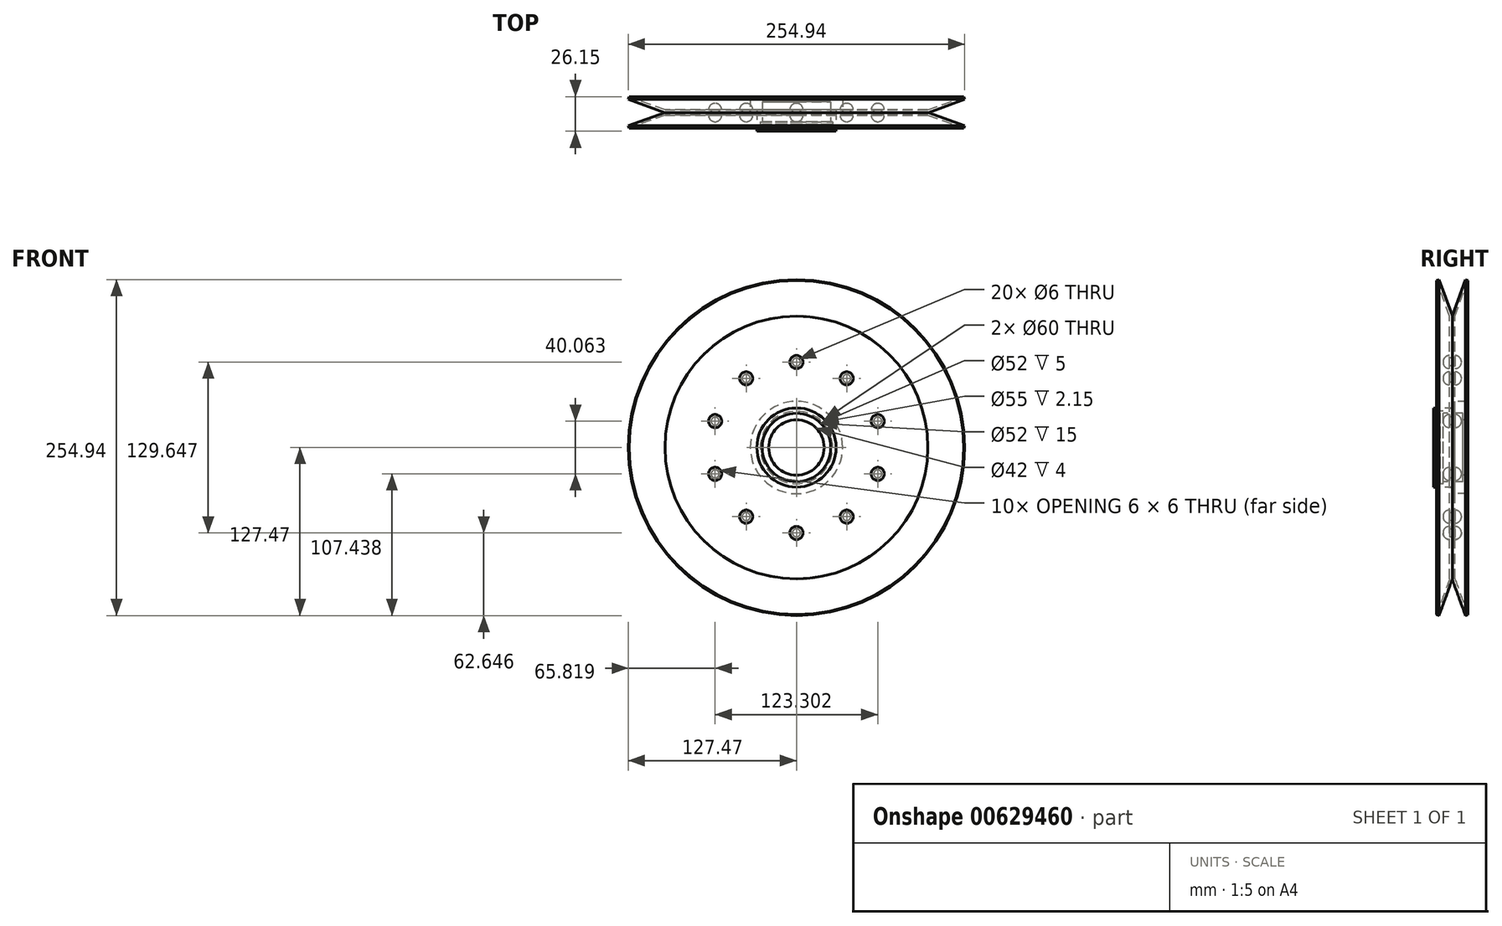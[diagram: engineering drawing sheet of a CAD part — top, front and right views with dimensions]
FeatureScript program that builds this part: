
annotation { "Feature Type Name" : "Feature", "Feature Type Description" : "" }
export const myFeature = defineFeature(function(context is Context, id is Id, definition is map)
    precondition{}
    {
        {
            var Q0;
            Q0=qCreatedBy(makeId("Right.planeOp"),FACE);
            var sketch = newSketch(context, id + "F0", { "sketchPlane" : qUnion([Q0])});
            skLineSegment(sketch, "E0", {"start": v(0, 0) * mm, "end": v(0, 100) * mm});
            skLineSegment(sketch, "E1", {"start": v(0, 100) * mm, "end": v(10, 127.47) * mm});
            skLineSegment(sketch, "E2.0", {"start": v(2, 99.65) * mm, "end": v(11.88, 126.8) * mm});
            skLineSegment(sketch, "E2.1", {"start": v(2, 0) * mm, "end": v(2, 99.65) * mm});
            skLineSegment(sketch, "E3", {"start": v(10, 127.47) * mm, "end": v(11.88, 126.8) * mm});
            skLineSegment(sketch, "E4", {"start": v(0, 0) * mm, "end": v(2, 0) * mm});
            skSolve(sketch);
        }
        {
            var Q0;
            Q0=makeQuery(id+"F0.imprint","IMPRINT",FACE,{"disambiguationData":[TD([[makeQuery(id+"F0.imprint","IMPRINT",EDGE,{"derivedFrom":sQuery(id+"F0.wireOp",EDGE,"E0")}),-1.0]])]});
            var Q1;
            Q1=sQuery(id+"F0.wireOp",EDGE,"E4");
            revolve(context, id + "F1", {"surfaceOperationType" : NewSurfaceOperationType.NEW, "entities" : qUnion([Q0]), "axis" : qUnion([Q1]), "revolveType" : RevolveType.FULL});
        }
        {
            var Q0;
            Q0=makeQuery(id+"F1.opRevolve","SWEPT_FACE",FACE,{"disambiguationData":[OSD([sQuery(id+"F0.wireOp",EDGE,"E2.1")])]});
            var sketch = newSketch(context, id + "F2", { "sketchPlane" : qUnion([Q0])});
            skPoint(sketch, "E5", {"position": v(0, 0) * mm});
            skSolve(sketch);
        }
        {
            var Q0;
            Q0=sQuery(id+"F2.wireOp",VERTEX,"E5");
            var Q1;
            Q1=makeQuery(id+"F1.opRevolve","SWEPT_BODY",BODY,{"disambiguationData":[OSD([sQuery(id+"F0.wireOp",EDGE,"E0"),sQuery(id+"F0.wireOp",EDGE,"E1"),sQuery(id+"F0.wireOp",EDGE,"E2.0"),sQuery(id+"F0.wireOp",EDGE,"E2.1"),sQuery(id+"F0.wireOp",EDGE,"E3"),sQuery(id+"F0.wireOp",EDGE,"E4")])]});
            hole(context, id + "F3", {"style" : HoleStyle.SIMPLE, "endStyle" : HoleEndStyle.THROUGH, "holeDiameter" : 60 * mm, "majorDiameter" : 10 * mm, "isTappedThrough" : true, "tappedDepth" : 25.5 * mm, "tapClearance" : 3, "locations" : qUnion([Q0]), "scope" : qUnion([Q1]), "startStyle" : HoleStartStyle.SKETCH});
        }
        {
            var Q0;
            Q0=makeQuery(id+"F1.opRevolve","SWEPT_FACE",FACE,{"disambiguationData":[OSD([sQuery(id+"F0.wireOp",EDGE,"E2.1")])]});
            var sketch = newSketch(context, id + "F4", { "sketchPlane" : qUnion([Q0])});
            skCircle(sketch, "E6.0.0", {"center": v(0, 0) * mm, "radius": 99.65 * mm});
            skLineSegment(sketch, "E7", {"start": v(0, 30) * mm, "end": v(0, 99.65) * mm, "construction": true});
            skCircle(sketch, "E8", {"center": v(0, 64.82) * mm, "radius": 3 * mm});
            skCircle(sketch, "E9.1.0", {"center": v(-38.1, 52.44) * mm, "radius": 3 * mm});
            skCircle(sketch, "E9.2.0", {"center": v(-61.65, 20.03) * mm, "radius": 3 * mm});
            skCircle(sketch, "E9.3.0", {"center": v(-61.65, -20.03) * mm, "radius": 3 * mm});
            skCircle(sketch, "E9.4.0", {"center": v(-38.1, -52.44) * mm, "radius": 3 * mm});
            skCircle(sketch, "E9.5.0", {"center": v(0, -64.82) * mm, "radius": 3 * mm});
            skCircle(sketch, "E9.6.0", {"center": v(38.1, -52.44) * mm, "radius": 3 * mm});
            skCircle(sketch, "E9.7.0", {"center": v(61.65, -20.03) * mm, "radius": 3 * mm});
            skCircle(sketch, "E9.8.0", {"center": v(61.65, 20.03) * mm, "radius": 3 * mm});
            skCircle(sketch, "E9.9.0", {"center": v(38.1, 52.44) * mm, "radius": 3 * mm});
            skSolve(sketch);
        }
        {
            var Q0;
            Q0=makeQuery(id+"F4.imprint","IMPRINT",FACE,{"disambiguationData":[TD([[makeQuery(id+"F4.imprint","IMPRINT",EDGE,{"derivedFrom":sQuery(id+"F4.wireOp",EDGE,"E8")}),1.0]])]});
            var Q1;
            Q1=makeQuery(id+"F4.imprint","IMPRINT",FACE,{"disambiguationData":[TD([[makeQuery(id+"F4.imprint","IMPRINT",EDGE,{"derivedFrom":sQuery(id+"F4.wireOp",EDGE,"E9.1.0")}),1.0]])]});
            var Q2;
            Q2=makeQuery(id+"F4.imprint","IMPRINT",FACE,{"disambiguationData":[TD([[makeQuery(id+"F4.imprint","IMPRINT",EDGE,{"derivedFrom":sQuery(id+"F4.wireOp",EDGE,"E9.2.0")}),1.0]])]});
            var Q3;
            Q3=makeQuery(id+"F4.imprint","IMPRINT",FACE,{"disambiguationData":[TD([[makeQuery(id+"F4.imprint","IMPRINT",EDGE,{"derivedFrom":sQuery(id+"F4.wireOp",EDGE,"E9.3.0")}),1.0]])]});
            var Q4;
            Q4=makeQuery(id+"F4.imprint","IMPRINT",FACE,{"disambiguationData":[TD([[makeQuery(id+"F4.imprint","IMPRINT",EDGE,{"derivedFrom":sQuery(id+"F4.wireOp",EDGE,"E9.4.0")}),1.0]])]});
            var Q5;
            Q5=makeQuery(id+"F4.imprint","IMPRINT",FACE,{"disambiguationData":[TD([[makeQuery(id+"F4.imprint","IMPRINT",EDGE,{"derivedFrom":sQuery(id+"F4.wireOp",EDGE,"E9.5.0")}),1.0]])]});
            var Q6;
            Q6=makeQuery(id+"F4.imprint","IMPRINT",FACE,{"disambiguationData":[TD([[makeQuery(id+"F4.imprint","IMPRINT",EDGE,{"derivedFrom":sQuery(id+"F4.wireOp",EDGE,"E9.6.0")}),1.0]])]});
            var Q7;
            Q7=makeQuery(id+"F4.imprint","IMPRINT",FACE,{"disambiguationData":[TD([[makeQuery(id+"F4.imprint","IMPRINT",EDGE,{"derivedFrom":sQuery(id+"F4.wireOp",EDGE,"E9.7.0")}),1.0]])]});
            var Q8;
            Q8=makeQuery(id+"F4.imprint","IMPRINT",FACE,{"disambiguationData":[TD([[makeQuery(id+"F4.imprint","IMPRINT",EDGE,{"derivedFrom":sQuery(id+"F4.wireOp",EDGE,"E9.8.0")}),1.0]])]});
            var Q9;
            Q9=makeQuery(id+"F4.imprint","IMPRINT",FACE,{"disambiguationData":[TD([[makeQuery(id+"F4.imprint","IMPRINT",EDGE,{"derivedFrom":sQuery(id+"F4.wireOp",EDGE,"E9.9.0")}),1.0]])]});
            extrude(context, id + "F5", {"entities" : qUnion([Q0, Q1, Q2, Q3, Q4, Q5, Q6, Q7, Q8, Q9]), "operationType" : NewBodyOperationType.REMOVE, "endBound" : BoundingType.THROUGH_ALL, "oppositeDirection" : true, "depth" : 25 * mm, "offsetDistance" : 25 * mm});
        }
        {
            var Q0;
            Q0=makeQuery(id+"F1.opRevolve","SWEPT_BODY",BODY,{"disambiguationData":[OSD([sQuery(id+"F0.wireOp",EDGE,"E0"),sQuery(id+"F0.wireOp",EDGE,"E1"),sQuery(id+"F0.wireOp",EDGE,"E2.0"),sQuery(id+"F0.wireOp",EDGE,"E2.1"),sQuery(id+"F0.wireOp",EDGE,"E3"),sQuery(id+"F0.wireOp",EDGE,"E4")])]});
            var Q1;
            Q1=makeQuery(id+"F1.opRevolve","SWEPT_FACE",FACE,{"disambiguationData":[OSD([sQuery(id+"F0.wireOp",EDGE,"E0")])]});
            mirror(context, id + "F6", {"entities" : qUnion([Q0]), "mirrorPlane" : qUnion([Q1])});
        }
        {
            var Q0;
            Q0=qCreatedBy(makeId("Right.planeOp"),FACE);
            var sketch = newSketch(context, id + "F7", { "sketchPlane" : qUnion([Q0])});
            skLineSegment(sketch, "E10", {"start": v(8.12, -116.47) * mm, "end": v(2, -99.65) * mm});
            skLineSegment(sketch, "E11", {"start": v(2, 99.65) * mm, "end": v(8.12, 116.47) * mm});
            skLineSegment(sketch, "E12", {"start": v(-8.12, 116.47) * mm, "end": v(-2, 99.65) * mm});
            skLineSegment(sketch, "E13", {"start": v(-2, -99.65) * mm, "end": v(-8.12, -116.47) * mm});
            skLineSegment(sketch, "E14", {"start": v(0, 67.82) * mm, "end": v(2, 67.82) * mm});
            skLineSegment(sketch, "E15", {"start": v(-2, 67.82) * mm, "end": v(0, 67.82) * mm});
            skLineSegment(sketch, "E16", {"start": v(2, 67.82) * mm, "end": v(2, 69.82) * mm});
            skLineSegment(sketch, "E17", {"start": v(-2, 67.82) * mm, "end": v(-2, 69.82) * mm});
            skLineSegment(sketch, "E18", {"start": v(-2, 67.82) * mm, "end": v(2, 67.82) * mm});
            skLineSegment(sketch, "E19", {"start": v(2, 67.82) * mm, "end": v(2, 64.82) * mm, "construction": true});
            skLineSegment(sketch, "E20", {"start": v(-2, 67.82) * mm, "end": v(-2, 64.82) * mm, "construction": true});
            skArc(sketch, "E21", {"start": v(7, 64.82) * mm, "mid": v(5.54, 68.36) * mm, "end": v(2, 69.82) * mm});
            skArc(sketch, "E22", {"start": v(-2, 69.82) * mm, "mid": v(-5.54, 68.36) * mm, "end": v(-7, 64.82) * mm});
            skLineSegment(sketch, "E23", {"start": v(-7, 64.82) * mm, "end": v(7, 64.82) * mm});
            skSolve(sketch);
        }
        {
            var Q0;
            Q0=makeQuery(id+"F7.imprint","IMPRINT",FACE,{"disambiguationData":[TD([[makeQuery(id+"F7.imprint","IMPRINT",EDGE,{"derivedFrom":sQuery(id+"F7.wireOp",EDGE,"E16")}),-1.0]])]});
            var Q1;
            Q1=sQuery(id+"F7.wireOp",EDGE,"E23");
            revolve(context, id + "F8", {"surfaceOperationType" : NewSurfaceOperationType.NEW, "entities" : qUnion([Q0]), "axis" : qUnion([Q1]), "revolveType" : RevolveType.FULL});
        }
        {
            var Q0;
            Q0=makeQuery(id+"F8.opRevolve","SWEPT_BODY",BODY,{"disambiguationData":[OSD([sQuery(id+"F7.wireOp",EDGE,"E16"),sQuery(id+"F7.wireOp",EDGE,"E17"),sQuery(id+"F7.wireOp",EDGE,"E18"),sQuery(id+"F7.wireOp",EDGE,"E21"),sQuery(id+"F7.wireOp",EDGE,"E22"),sQuery(id+"F7.wireOp",EDGE,"E23")])]});
            var Q1;
            Q1=makeQuery(id+"F1.opRevolve","SWEPT_FACE",FACE,{"disambiguationData":[OSD([sQuery(id+"F0.wireOp",EDGE,"E2.0")])]});
            circularPattern(context, id + "F9", {"entities" : qUnion([Q0]), "axis" : qUnion([Q1]), "angle" : 360 * degree, "instanceCount" : 10, "equalSpace" : true, "computeTransformsWithoutBuiltin" : true});
        }
        {
            var Q0;
            Q0=qCreatedBy(makeId("Right.planeOp"),FACE);
            var sketch = newSketch(context, id + "F10", { "sketchPlane" : qUnion([Q0])});
            skLineSegment(sketch, "E24.0", {"start": v(2, 30) * mm, "end": v(2, -30) * mm, "construction": true});
            skLineSegment(sketch, "E25.0", {"start": v(0, -30) * mm, "end": v(0, 30) * mm, "construction": true});
            skLineSegment(sketch, "E26", {"start": v(2, 30) * mm, "end": v(2, 35) * mm});
            skLineSegment(sketch, "E27", {"start": v(2, 35) * mm, "end": v(12, 35) * mm});
            skLineSegment(sketch, "E28", {"start": v(12, 35) * mm, "end": v(12, 21) * mm});
            skLineSegment(sketch, "E29", {"start": v(12, 21) * mm, "end": v(8, 21) * mm});
            skLineSegment(sketch, "E30", {"start": v(8, 21) * mm, "end": v(8, 26) * mm});
            skLineSegment(sketch, "E31", {"start": v(8, 26) * mm, "end": v(-7, 26) * mm});
            skLineSegment(sketch, "E32", {"start": v(-7, 26) * mm, "end": v(-7, 27.5) * mm});
            skLineSegment(sketch, "E33", {"start": v(-7, 27.5) * mm, "end": v(-9.15, 27.5) * mm});
            skLineSegment(sketch, "E34", {"start": v(-9.15, 27.5) * mm, "end": v(-9.15, 26) * mm});
            skLineSegment(sketch, "E35", {"start": v(-9.15, 26) * mm, "end": v(-14.15, 26) * mm});
            skLineSegment(sketch, "E36", {"start": v(-14.15, 26) * mm, "end": v(-14.15, 30) * mm});
            skLineSegment(sketch, "E37", {"start": v(-14.15, 30) * mm, "end": v(2, 30) * mm});
            skSolve(sketch);
        }
        {
            var Q0;
            Q0=qCreatedBy(makeId("Right.planeOp"),FACE);
            var sketch = newSketch(context, id + "F11", { "sketchPlane" : qUnion([Q0])});
            skLineSegment(sketch, "E38", {"start": v(-17.05, 0) * mm, "end": v(15.8, 0) * mm, "construction": true});
            skSolve(sketch);
        }
        {
            var Q0;
            Q0=makeQuery(id+"F10.imprint","IMPRINT",FACE,{"disambiguationData":[TD([[makeQuery(id+"F10.imprint","IMPRINT",EDGE,{"derivedFrom":sQuery(id+"F10.wireOp",EDGE,"E26")}),-1.0]])]});
            var Q1;
            Q1=sQuery(id+"F11.wireOp",EDGE,"E38");
            revolve(context, id + "F12", {"surfaceOperationType" : NewSurfaceOperationType.NEW, "entities" : qUnion([Q0]), "axis" : qUnion([Q1]), "revolveType" : RevolveType.FULL});
        }
    });
